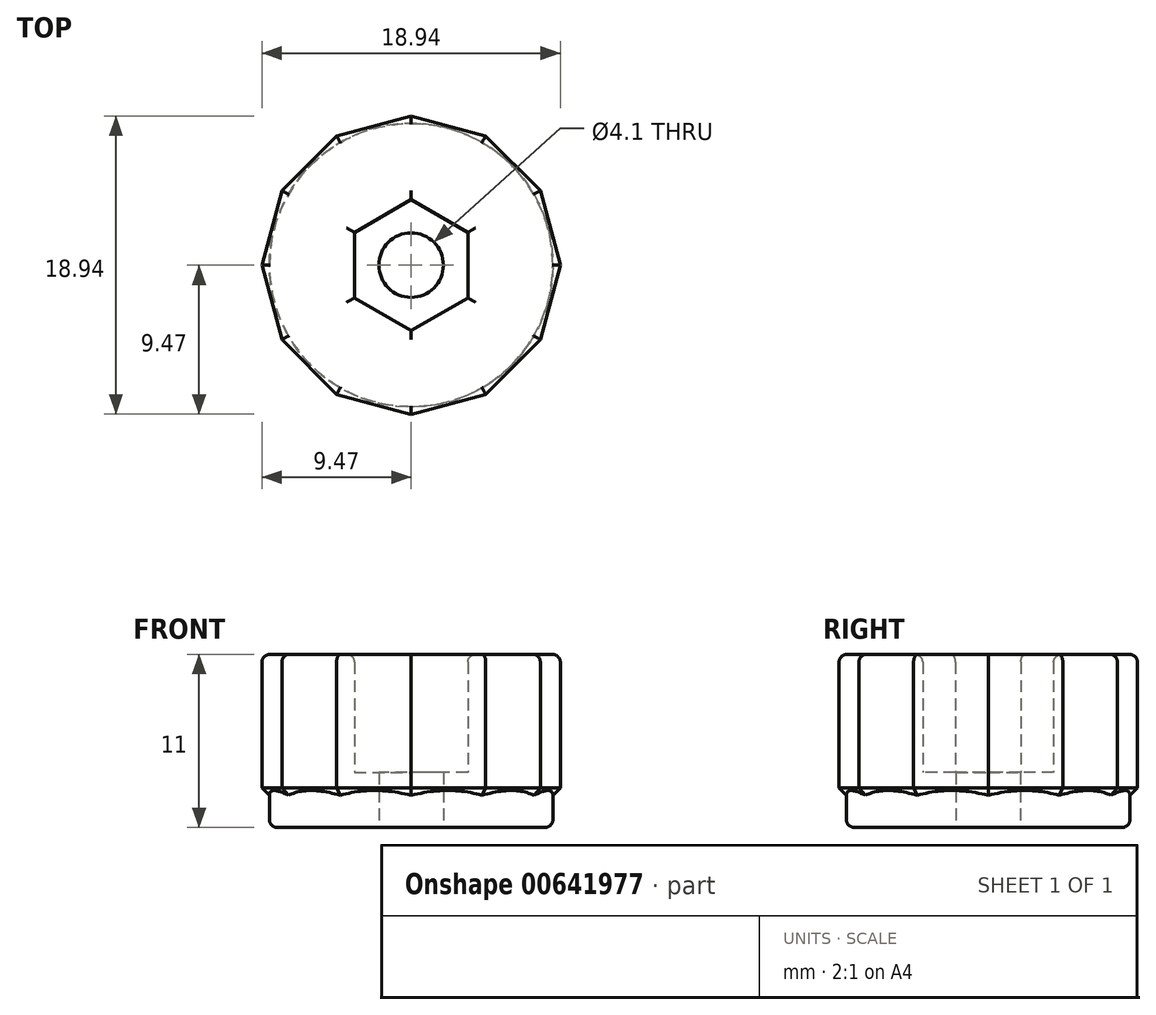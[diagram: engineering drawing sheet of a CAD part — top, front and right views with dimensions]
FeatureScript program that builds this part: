
annotation { "Feature Type Name" : "Feature", "Feature Type Description" : "" }
export const myFeature = defineFeature(function(context is Context, id is Id, definition is map)
    precondition{}
    {
        {
            var Q0;
            Q0=qCreatedBy(makeId("Top.planeOp"),FACE);
            var sketch = newSketch(context, id + "F0", { "sketchPlane" : qUnion([Q0])});
            skCircle(sketch, "E0.cCircle", {"center": v(0, 0) * mm, "radius": 4.16 * mm, "construction": true});
            skLineSegment(sketch, "E0.0", {"start": v(3.6, -2.08) * mm, "end": v(0, -4.16) * mm});
            skLineSegment(sketch, "E0.1", {"start": v(0, -4.16) * mm, "end": v(-3.6, -2.08) * mm});
            skLineSegment(sketch, "E0.2", {"start": v(-3.6, -2.08) * mm, "end": v(-3.6, 2.08) * mm});
            skLineSegment(sketch, "E0.3", {"start": v(-3.6, 2.08) * mm, "end": v(0, 4.16) * mm});
            skLineSegment(sketch, "E0.4", {"start": v(0, 4.16) * mm, "end": v(3.6, 2.08) * mm});
            skLineSegment(sketch, "E0.5", {"start": v(3.6, 2.08) * mm, "end": v(3.6, -2.08) * mm});
            skCircle(sketch, "E1", {"center": v(0, 0) * mm, "radius": 9 * mm});
            skCircle(sketch, "E2", {"center": v(0, 0) * mm, "radius": 7.5 * mm});
            skCircle(sketch, "E3.cCircle", {"center": v(0, 0) * mm, "radius": 9.47 * mm, "construction": true});
            skLineSegment(sketch, "E3.0", {"start": v(8.2, -4.74) * mm, "end": v(4.74, -8.2) * mm});
            skLineSegment(sketch, "E3.1", {"start": v(4.74, -8.2) * mm, "end": v(0, -9.47) * mm});
            skLineSegment(sketch, "E3.2", {"start": v(0, -9.47) * mm, "end": v(-4.74, -8.2) * mm});
            skLineSegment(sketch, "E3.3", {"start": v(-4.74, -8.2) * mm, "end": v(-8.2, -4.74) * mm});
            skLineSegment(sketch, "E3.4", {"start": v(-8.2, -4.74) * mm, "end": v(-9.47, 0) * mm});
            skLineSegment(sketch, "E3.5", {"start": v(-9.47, 0) * mm, "end": v(-8.2, 4.74) * mm});
            skLineSegment(sketch, "E3.6", {"start": v(-8.2, 4.74) * mm, "end": v(-4.74, 8.2) * mm});
            skLineSegment(sketch, "E3.7", {"start": v(-4.74, 8.2) * mm, "end": v(0, 9.47) * mm});
            skLineSegment(sketch, "E3.8", {"start": v(0, 9.47) * mm, "end": v(4.74, 8.2) * mm});
            skLineSegment(sketch, "E3.9", {"start": v(4.74, 8.2) * mm, "end": v(8.2, 4.74) * mm});
            skLineSegment(sketch, "E3.10", {"start": v(8.2, 4.74) * mm, "end": v(9.47, 0) * mm});
            skLineSegment(sketch, "E3.11", {"start": v(9.47, 0) * mm, "end": v(8.2, -4.74) * mm});
            skCircle(sketch, "E4", {"center": v(0, 0) * mm, "radius": 2.05 * mm});
            skSolve(sketch);
        }
        {
            var Q0;
            Q0=makeQuery(id+"F0.imprint","IMPRINT",FACE,{"disambiguationData":[TD([[makeQuery(id+"F0.imprint","IMPRINT",EDGE,{"derivedFrom":sQuery(id+"F0.wireOp",EDGE,"E1")}),1.0]])]});
            var Q1;
            Q1=makeQuery(id+"F0.imprint","IMPRINT",FACE,{"disambiguationData":[TD([[makeQuery(id+"F0.imprint","IMPRINT",EDGE,{"derivedFrom":sQuery(id+"F0.wireOp",EDGE,"E1")}),-1.0]])]});
            var Q2;
            Q2=makeQuery(id+"F0.imprint","IMPRINT",FACE,{"disambiguationData":[TD([[makeQuery(id+"F0.imprint","IMPRINT",EDGE,{"derivedFrom":sQuery(id+"F0.wireOp",EDGE,"E0.0")}),1.0]])]});
            var Q3;
            Q3=makeQuery(id+"F0.imprint","IMPRINT",FACE,{"disambiguationData":[TD([[makeQuery(id+"F0.imprint","IMPRINT",EDGE,{"derivedFrom":sQuery(id+"F0.wireOp",EDGE,"E0.0")}),-1.0]])]});
            extrude(context, id + "F1", {"entities" : qUnion([Q0, Q1, Q2, Q3]), "depth" : 11 * mm, "offsetDistance" : 25 * mm, "hasSecondDirection" : true, "secondDirectionOppositeDirection" : false, "secondDirectionDepth" : 2 * mm});
        }
        {
            var Q0;
            Q0=makeQuery(id+"F0.imprint","IMPRINT",FACE,{"disambiguationData":[TD([[makeQuery(id+"F0.imprint","IMPRINT",EDGE,{"derivedFrom":sQuery(id+"F0.wireOp",EDGE,"E1")}),1.0]])]});
            var Q1;
            Q1=makeQuery(id+"F0.imprint","IMPRINT",FACE,{"disambiguationData":[TD([[makeQuery(id+"F0.imprint","IMPRINT",EDGE,{"derivedFrom":sQuery(id+"F0.wireOp",EDGE,"E0.0")}),1.0]])]});
            var Q2;
            Q2=makeQuery(id+"F0.imprint","IMPRINT",FACE,{"disambiguationData":[TD([[makeQuery(id+"F0.imprint","IMPRINT",EDGE,{"derivedFrom":sQuery(id+"F0.wireOp",EDGE,"E0.0")}),-1.0]])]});
            extrude(context, id + "F2", {"entities" : qUnion([Q0, Q1, Q2]), "operationType" : NewBodyOperationType.ADD, "depth" : 11 * mm, "offsetDistance" : 25 * mm});
        }
        {
            var Q0;
            Q0=makeQuery(id+"F0.imprint","IMPRINT",FACE,{"disambiguationData":[TD([[makeQuery(id+"F0.imprint","IMPRINT",EDGE,{"derivedFrom":sQuery(id+"F0.wireOp",EDGE,"E0.0")}),-1.0]])]});
            var Q1;
            Q1=makeQuery(id+"F1.opExtrude","CAP_FACE",FACE,{"disambiguationData":[OSD([sQuery(id+"F0.wireOp",EDGE,"E3.0"),sQuery(id+"F0.wireOp",EDGE,"E3.1"),sQuery(id+"F0.wireOp",EDGE,"E3.2"),sQuery(id+"F0.wireOp",EDGE,"E3.3"),sQuery(id+"F0.wireOp",EDGE,"E3.4"),sQuery(id+"F0.wireOp",EDGE,"E3.5"),sQuery(id+"F0.wireOp",EDGE,"E3.6"),sQuery(id+"F0.wireOp",EDGE,"E3.7"),sQuery(id+"F0.wireOp",EDGE,"E3.8"),sQuery(id+"F0.wireOp",EDGE,"E3.9"),sQuery(id+"F0.wireOp",EDGE,"E3.10"),sQuery(id+"F0.wireOp",EDGE,"E3.11")])],"isStart":false});
            extrude(context, id + "F3", {"entities" : qUnion([Q0, Q1]), "operationType" : NewBodyOperationType.REMOVE, "depth" : 20 * mm, "offsetDistance" : 25 * mm});
        }
        {
            var Q0;
            Q0=makeQuery(id+"F0.imprint","IMPRINT",FACE,{"disambiguationData":[TD([[makeQuery(id+"F0.imprint","IMPRINT",EDGE,{"derivedFrom":sQuery(id+"F0.wireOp",EDGE,"E0.0")}),-1.0]])]});
            extrude(context, id + "F4", {"entities" : qUnion([Q0]), "operationType" : NewBodyOperationType.ADD, "depth" : 3.5 * mm, "offsetDistance" : 25 * mm});
        }
        {
            var Q0;
            Q0=makeQuery(id+"F0.imprint","IMPRINT",FACE,{"disambiguationData":[TD([[makeQuery(id+"F0.imprint","IMPRINT",EDGE,{"derivedFrom":sQuery(id+"F0.wireOp",EDGE,"E4")}),1.0]])]});
            extrude(context, id + "F5", {"entities" : qUnion([Q0]), "operationType" : NewBodyOperationType.REMOVE, "depth" : 11 * mm, "offsetDistance" : 25 * mm});
        }
        {
            var Q0;
            Q0=makeQuery(id+"F1.opExtrude","CAP_EDGE",EDGE,{"disambiguationData":[OSD([sQuery(id+"F0.wireOp",EDGE,"E3.0")])],"isStart":true});
            var Q1;
            Q1=makeQuery(id+"F1.opExtrude","CAP_EDGE",EDGE,{"disambiguationData":[OSD([sQuery(id+"F0.wireOp",EDGE,"E3.11")])],"isStart":true});
            var Q2;
            Q2=makeQuery(id+"F1.opExtrude","CAP_EDGE",EDGE,{"disambiguationData":[OSD([sQuery(id+"F0.wireOp",EDGE,"E3.9")])],"isStart":true});
            var Q3;
            Q3=makeQuery(id+"F1.opExtrude","CAP_EDGE",EDGE,{"disambiguationData":[OSD([sQuery(id+"F0.wireOp",EDGE,"E3.8")])],"isStart":true});
            var Q4;
            Q4=makeQuery(id+"F1.opExtrude","CAP_EDGE",EDGE,{"disambiguationData":[OSD([sQuery(id+"F0.wireOp",EDGE,"E3.6")])],"isStart":true});
            var Q5;
            Q5=makeQuery(id+"F1.opExtrude","CAP_EDGE",EDGE,{"disambiguationData":[OSD([sQuery(id+"F0.wireOp",EDGE,"E3.5")])],"isStart":true});
            var Q6;
            Q6=makeQuery(id+"F1.opExtrude","CAP_EDGE",EDGE,{"disambiguationData":[OSD([sQuery(id+"F0.wireOp",EDGE,"E3.3")])],"isStart":true});
            var Q7;
            Q7=makeQuery(id+"F1.opExtrude","CAP_EDGE",EDGE,{"disambiguationData":[OSD([sQuery(id+"F0.wireOp",EDGE,"E3.2")])],"isStart":true});
            chamfer(context, id + "F6", {"entities" : qUnion([Q0, Q1, Q2, Q3, Q4, Q5, Q6, Q7]), "width" : .5 * mm, "tangentPropagation" : true});
        }
        {
            var Q0;
            Q0=makeQuery(id+"F1.opExtrude","CAP_EDGE",EDGE,{"disambiguationData":[OSD([sQuery(id+"F0.wireOp",EDGE,"E3.1")])],"isStart":true});
            var Q1;
            Q1=makeQuery(id+"F1.opExtrude","CAP_EDGE",EDGE,{"disambiguationData":[OSD([sQuery(id+"F0.wireOp",EDGE,"E3.10")])],"isStart":true});
            var Q2;
            Q2=makeQuery(id+"F1.opExtrude","CAP_EDGE",EDGE,{"disambiguationData":[OSD([sQuery(id+"F0.wireOp",EDGE,"E3.7")])],"isStart":true});
            var Q3;
            Q3=makeQuery(id+"F1.opExtrude","CAP_EDGE",EDGE,{"disambiguationData":[OSD([sQuery(id+"F0.wireOp",EDGE,"E3.4")])],"isStart":true});
            chamfer(context, id + "F7", {"entities" : qUnion([Q0, Q1, Q2, Q3]), "width" : .5 * mm, "tangentPropagation" : true});
        }
        {
            var Q0;
            Q0=makeQuery(id+"F2.opExtrude","CAP_EDGE",EDGE,{"disambiguationData":[OSD([sQuery(id+"F0.wireOp",EDGE,"E1")])],"isStart":true});
            var Q1;
            Q1=makeQuery(id+"F1.opExtrude","CAP_EDGE",EDGE,{"disambiguationData":[OSD([sQuery(id+"F0.wireOp",EDGE,"E3.1")])],"isStart":false});
            var Q2;
            Q2=makeQuery(id+"F1.opExtrude","CAP_EDGE",EDGE,{"disambiguationData":[OSD([sQuery(id+"F0.wireOp",EDGE,"E3.0")])],"isStart":false});
            var Q3;
            Q3=makeQuery(id+"F1.opExtrude","CAP_EDGE",EDGE,{"disambiguationData":[OSD([sQuery(id+"F0.wireOp",EDGE,"E3.11")])],"isStart":false});
            var Q4;
            Q4=makeQuery(id+"F1.opExtrude","CAP_EDGE",EDGE,{"disambiguationData":[OSD([sQuery(id+"F0.wireOp",EDGE,"E3.10")])],"isStart":false});
            var Q5;
            Q5=makeQuery(id+"F1.opExtrude","CAP_EDGE",EDGE,{"disambiguationData":[OSD([sQuery(id+"F0.wireOp",EDGE,"E3.9")])],"isStart":false});
            var Q6;
            Q6=makeQuery(id+"F1.opExtrude","CAP_EDGE",EDGE,{"disambiguationData":[OSD([sQuery(id+"F0.wireOp",EDGE,"E3.8")])],"isStart":false});
            var Q7;
            Q7=makeQuery(id+"F1.opExtrude","CAP_EDGE",EDGE,{"disambiguationData":[OSD([sQuery(id+"F0.wireOp",EDGE,"E3.7")])],"isStart":false});
            var Q8;
            Q8=makeQuery(id+"F1.opExtrude","CAP_EDGE",EDGE,{"disambiguationData":[OSD([sQuery(id+"F0.wireOp",EDGE,"E3.6")])],"isStart":false});
            var Q9;
            Q9=makeQuery(id+"F1.opExtrude","CAP_EDGE",EDGE,{"disambiguationData":[OSD([sQuery(id+"F0.wireOp",EDGE,"E3.5")])],"isStart":false});
            var Q10;
            Q10=makeQuery(id+"F1.opExtrude","CAP_EDGE",EDGE,{"disambiguationData":[OSD([sQuery(id+"F0.wireOp",EDGE,"E3.4")])],"isStart":false});
            var Q11;
            Q11=makeQuery(id+"F1.opExtrude","CAP_EDGE",EDGE,{"disambiguationData":[OSD([sQuery(id+"F0.wireOp",EDGE,"E3.3")])],"isStart":false});
            var Q12;
            Q12=makeQuery(id+"F1.opExtrude","CAP_EDGE",EDGE,{"disambiguationData":[OSD([sQuery(id+"F0.wireOp",EDGE,"E3.2")])],"isStart":false});
            fillet(context, id + "F8", {"entities" : qUnion([Q0, Q1, Q2, Q3, Q4, Q5, Q6, Q7, Q8, Q9, Q10, Q11, Q12]), "radius" : .5 * mm, "tangentPropagation" : true, "allowEdgeOverflow" : false});
        }
        {
            var Q0;
            {var subQ0=sQuery(id+"F0.wireOp",EDGE,"E4");var subQ1=sQuery(id+"F0.wireOp",EDGE,"E3.11");var subQ2=sQuery(id+"F0.wireOp",EDGE,"E3.10");var subQ3=sQuery(id+"F0.wireOp",EDGE,"E3.9");var subQ4=sQuery(id+"F0.wireOp",EDGE,"E3.8");var subQ5=sQuery(id+"F0.wireOp",EDGE,"E3.7");var subQ6=sQuery(id+"F0.wireOp",EDGE,"E3.6");var subQ7=sQuery(id+"F0.wireOp",EDGE,"E3.5");var subQ8=sQuery(id+"F0.wireOp",EDGE,"E3.4");var subQ9=sQuery(id+"F0.wireOp",EDGE,"E3.3");var subQ10=sQuery(id+"F0.wireOp",EDGE,"E3.2");var subQ11=sQuery(id+"F0.wireOp",EDGE,"E3.1");var subQ12=sQuery(id+"F0.wireOp",EDGE,"E3.0");Q0=makeQuery(id+"F3.boolean.opBoolean","INTERSECT",EDGE,{"derivedFrom":[makeQuery(id+"F1.opExtrude","CAP_FACE",FACE,{"disambiguationData":[OSD([subQ12,subQ11,subQ10,subQ9,subQ8,subQ7,subQ6,subQ5,subQ4,subQ3,subQ2,subQ1,subQ0])],"isStart":false}),makeQuery(id+"F3.opExtrude","SWEPT_FACE",FACE,{"disambiguationData":[OSD([sQuery(id+"F0.wireOp",EDGE,"E0.3")])]}),makeQuery(id+"F3.opExtrude","CAP_FACE",FACE,{"disambiguationData":[OSD([subQ12,subQ11,subQ10,subQ9,subQ8,subQ7,subQ6,subQ5,subQ4,subQ3,subQ2,subQ1,subQ0])],"isStart":true})]});}
            var Q1;
            {var subQ0=sQuery(id+"F0.wireOp",EDGE,"E4");var subQ1=sQuery(id+"F0.wireOp",EDGE,"E3.11");var subQ2=sQuery(id+"F0.wireOp",EDGE,"E3.10");var subQ3=sQuery(id+"F0.wireOp",EDGE,"E3.9");var subQ4=sQuery(id+"F0.wireOp",EDGE,"E3.8");var subQ5=sQuery(id+"F0.wireOp",EDGE,"E3.7");var subQ6=sQuery(id+"F0.wireOp",EDGE,"E3.6");var subQ7=sQuery(id+"F0.wireOp",EDGE,"E3.5");var subQ8=sQuery(id+"F0.wireOp",EDGE,"E3.4");var subQ9=sQuery(id+"F0.wireOp",EDGE,"E3.3");var subQ10=sQuery(id+"F0.wireOp",EDGE,"E3.2");var subQ11=sQuery(id+"F0.wireOp",EDGE,"E3.1");var subQ12=sQuery(id+"F0.wireOp",EDGE,"E3.0");Q1=makeQuery(id+"F3.boolean.opBoolean","INTERSECT",EDGE,{"derivedFrom":[makeQuery(id+"F1.opExtrude","CAP_FACE",FACE,{"disambiguationData":[OSD([subQ12,subQ11,subQ10,subQ9,subQ8,subQ7,subQ6,subQ5,subQ4,subQ3,subQ2,subQ1,subQ0])],"isStart":false}),makeQuery(id+"F3.opExtrude","SWEPT_FACE",FACE,{"disambiguationData":[OSD([sQuery(id+"F0.wireOp",EDGE,"E0.4")])]}),makeQuery(id+"F3.opExtrude","CAP_FACE",FACE,{"disambiguationData":[OSD([subQ12,subQ11,subQ10,subQ9,subQ8,subQ7,subQ6,subQ5,subQ4,subQ3,subQ2,subQ1,subQ0])],"isStart":true})]});}
            var Q2;
            {var subQ0=sQuery(id+"F0.wireOp",EDGE,"E4");var subQ1=sQuery(id+"F0.wireOp",EDGE,"E3.11");var subQ2=sQuery(id+"F0.wireOp",EDGE,"E3.10");var subQ3=sQuery(id+"F0.wireOp",EDGE,"E3.9");var subQ4=sQuery(id+"F0.wireOp",EDGE,"E3.8");var subQ5=sQuery(id+"F0.wireOp",EDGE,"E3.7");var subQ6=sQuery(id+"F0.wireOp",EDGE,"E3.6");var subQ7=sQuery(id+"F0.wireOp",EDGE,"E3.5");var subQ8=sQuery(id+"F0.wireOp",EDGE,"E3.4");var subQ9=sQuery(id+"F0.wireOp",EDGE,"E3.3");var subQ10=sQuery(id+"F0.wireOp",EDGE,"E3.2");var subQ11=sQuery(id+"F0.wireOp",EDGE,"E3.1");var subQ12=sQuery(id+"F0.wireOp",EDGE,"E3.0");Q2=makeQuery(id+"F3.boolean.opBoolean","INTERSECT",EDGE,{"derivedFrom":[makeQuery(id+"F1.opExtrude","CAP_FACE",FACE,{"disambiguationData":[OSD([subQ12,subQ11,subQ10,subQ9,subQ8,subQ7,subQ6,subQ5,subQ4,subQ3,subQ2,subQ1,subQ0])],"isStart":false}),makeQuery(id+"F3.opExtrude","SWEPT_FACE",FACE,{"disambiguationData":[OSD([sQuery(id+"F0.wireOp",EDGE,"E0.5")])]}),makeQuery(id+"F3.opExtrude","CAP_FACE",FACE,{"disambiguationData":[OSD([subQ12,subQ11,subQ10,subQ9,subQ8,subQ7,subQ6,subQ5,subQ4,subQ3,subQ2,subQ1,subQ0])],"isStart":true})]});}
            var Q3;
            {var subQ0=sQuery(id+"F0.wireOp",EDGE,"E4");var subQ1=sQuery(id+"F0.wireOp",EDGE,"E3.11");var subQ2=sQuery(id+"F0.wireOp",EDGE,"E3.10");var subQ3=sQuery(id+"F0.wireOp",EDGE,"E3.9");var subQ4=sQuery(id+"F0.wireOp",EDGE,"E3.8");var subQ5=sQuery(id+"F0.wireOp",EDGE,"E3.7");var subQ6=sQuery(id+"F0.wireOp",EDGE,"E3.6");var subQ7=sQuery(id+"F0.wireOp",EDGE,"E3.5");var subQ8=sQuery(id+"F0.wireOp",EDGE,"E3.4");var subQ9=sQuery(id+"F0.wireOp",EDGE,"E3.3");var subQ10=sQuery(id+"F0.wireOp",EDGE,"E3.2");var subQ11=sQuery(id+"F0.wireOp",EDGE,"E3.1");var subQ12=sQuery(id+"F0.wireOp",EDGE,"E3.0");Q3=makeQuery(id+"F3.boolean.opBoolean","INTERSECT",EDGE,{"derivedFrom":[makeQuery(id+"F1.opExtrude","CAP_FACE",FACE,{"disambiguationData":[OSD([subQ12,subQ11,subQ10,subQ9,subQ8,subQ7,subQ6,subQ5,subQ4,subQ3,subQ2,subQ1,subQ0])],"isStart":false}),makeQuery(id+"F3.opExtrude","SWEPT_FACE",FACE,{"disambiguationData":[OSD([sQuery(id+"F0.wireOp",EDGE,"E0.0")])]}),makeQuery(id+"F3.opExtrude","CAP_FACE",FACE,{"disambiguationData":[OSD([subQ12,subQ11,subQ10,subQ9,subQ8,subQ7,subQ6,subQ5,subQ4,subQ3,subQ2,subQ1,subQ0])],"isStart":true})]});}
            var Q4;
            {var subQ0=sQuery(id+"F0.wireOp",EDGE,"E4");var subQ1=sQuery(id+"F0.wireOp",EDGE,"E3.11");var subQ2=sQuery(id+"F0.wireOp",EDGE,"E3.10");var subQ3=sQuery(id+"F0.wireOp",EDGE,"E3.9");var subQ4=sQuery(id+"F0.wireOp",EDGE,"E3.8");var subQ5=sQuery(id+"F0.wireOp",EDGE,"E3.7");var subQ6=sQuery(id+"F0.wireOp",EDGE,"E3.6");var subQ7=sQuery(id+"F0.wireOp",EDGE,"E3.5");var subQ8=sQuery(id+"F0.wireOp",EDGE,"E3.4");var subQ9=sQuery(id+"F0.wireOp",EDGE,"E3.3");var subQ10=sQuery(id+"F0.wireOp",EDGE,"E3.2");var subQ11=sQuery(id+"F0.wireOp",EDGE,"E3.1");var subQ12=sQuery(id+"F0.wireOp",EDGE,"E3.0");Q4=makeQuery(id+"F3.boolean.opBoolean","INTERSECT",EDGE,{"derivedFrom":[makeQuery(id+"F1.opExtrude","CAP_FACE",FACE,{"disambiguationData":[OSD([subQ12,subQ11,subQ10,subQ9,subQ8,subQ7,subQ6,subQ5,subQ4,subQ3,subQ2,subQ1,subQ0])],"isStart":false}),makeQuery(id+"F3.opExtrude","SWEPT_FACE",FACE,{"disambiguationData":[OSD([sQuery(id+"F0.wireOp",EDGE,"E0.1")])]}),makeQuery(id+"F3.opExtrude","CAP_FACE",FACE,{"disambiguationData":[OSD([subQ12,subQ11,subQ10,subQ9,subQ8,subQ7,subQ6,subQ5,subQ4,subQ3,subQ2,subQ1,subQ0])],"isStart":true})]});}
            var Q5;
            {var subQ0=sQuery(id+"F0.wireOp",EDGE,"E4");var subQ1=sQuery(id+"F0.wireOp",EDGE,"E3.11");var subQ2=sQuery(id+"F0.wireOp",EDGE,"E3.10");var subQ3=sQuery(id+"F0.wireOp",EDGE,"E3.9");var subQ4=sQuery(id+"F0.wireOp",EDGE,"E3.8");var subQ5=sQuery(id+"F0.wireOp",EDGE,"E3.7");var subQ6=sQuery(id+"F0.wireOp",EDGE,"E3.6");var subQ7=sQuery(id+"F0.wireOp",EDGE,"E3.5");var subQ8=sQuery(id+"F0.wireOp",EDGE,"E3.4");var subQ9=sQuery(id+"F0.wireOp",EDGE,"E3.3");var subQ10=sQuery(id+"F0.wireOp",EDGE,"E3.2");var subQ11=sQuery(id+"F0.wireOp",EDGE,"E3.1");var subQ12=sQuery(id+"F0.wireOp",EDGE,"E3.0");Q5=makeQuery(id+"F3.boolean.opBoolean","INTERSECT",EDGE,{"derivedFrom":[makeQuery(id+"F1.opExtrude","CAP_FACE",FACE,{"disambiguationData":[OSD([subQ12,subQ11,subQ10,subQ9,subQ8,subQ7,subQ6,subQ5,subQ4,subQ3,subQ2,subQ1,subQ0])],"isStart":false}),makeQuery(id+"F3.opExtrude","SWEPT_FACE",FACE,{"disambiguationData":[OSD([sQuery(id+"F0.wireOp",EDGE,"E0.2")])]}),makeQuery(id+"F3.opExtrude","CAP_FACE",FACE,{"disambiguationData":[OSD([subQ12,subQ11,subQ10,subQ9,subQ8,subQ7,subQ6,subQ5,subQ4,subQ3,subQ2,subQ1,subQ0])],"isStart":true})]});}
            fillet(context, id + "F9", {"entities" : qUnion([Q0, Q1, Q2, Q3, Q4, Q5]), "radius" : .5 * mm, "tangentPropagation" : true, "allowEdgeOverflow" : false});
        }
    });
